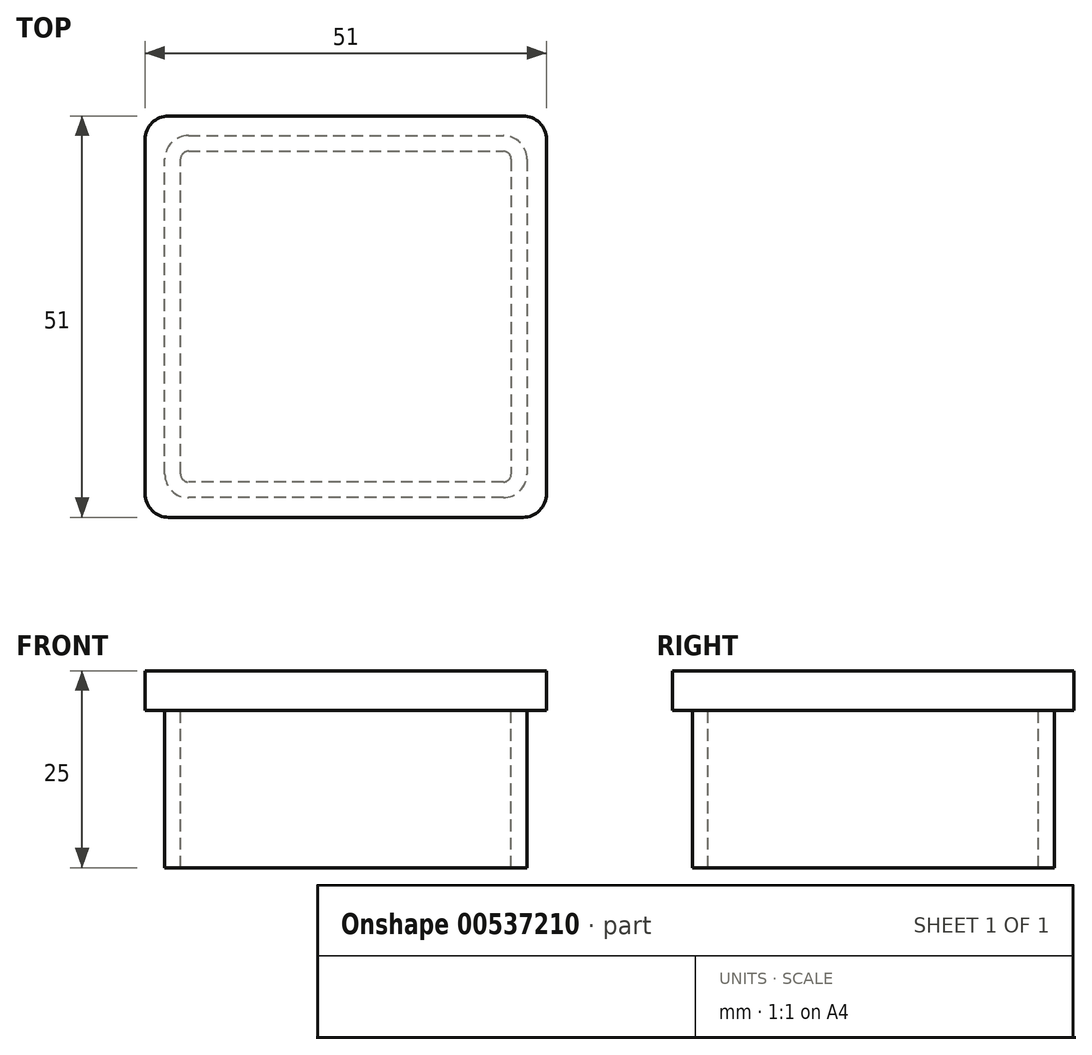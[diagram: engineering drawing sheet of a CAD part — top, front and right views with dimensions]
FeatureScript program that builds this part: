
annotation { "Feature Type Name" : "Feature", "Feature Type Description" : "" }
export const myFeature = defineFeature(function(context is Context, id is Id, definition is map)
    precondition{}
    {
        {
            var Q0;
            Q0=qCreatedBy(makeId("Top.planeOp"),FACE);
            var sketch = newSketch(context, id + "F0", { "sketchPlane" : qUnion([Q0])});
            skLineSegment(sketch, "E0.bottom", {"start": v(-22.5, -25.5) * mm, "end": v(22.5, -25.5) * mm});
            skLineSegment(sketch, "E0.top", {"start": v(-22.5, 25.5) * mm, "end": v(22.5, 25.5) * mm});
            skLineSegment(sketch, "E0.left", {"start": v(-25.5, -22.5) * mm, "end": v(-25.5, 22.5) * mm});
            skLineSegment(sketch, "E0.right", {"start": v(25.5, -22.5) * mm, "end": v(25.5, 22.5) * mm});
            skPoint(sketch, "E1.visualSharp", {"position": v(-25.5, 25.5) * mm});
            skArc(sketch, "E1.filletArc", {"start": v(-22.5, 25.5) * mm, "mid": v(-24.62, 24.62) * mm, "end": v(-25.5, 22.5) * mm});
            skPoint(sketch, "E2.visualSharp", {"position": v(25.5, 25.5) * mm});
            skArc(sketch, "E2.filletArc", {"start": v(25.5, 22.5) * mm, "mid": v(24.62, 24.62) * mm, "end": v(22.5, 25.5) * mm});
            skPoint(sketch, "E3.visualSharp", {"position": v(25.5, -25.5) * mm});
            skArc(sketch, "E3.filletArc", {"start": v(22.5, -25.5) * mm, "mid": v(24.62, -24.62) * mm, "end": v(25.5, -22.5) * mm});
            skPoint(sketch, "E4.visualSharp", {"position": v(-25.5, -25.5) * mm});
            skArc(sketch, "E4.filletArc", {"start": v(-25.5, -22.5) * mm, "mid": v(-24.62, -24.62) * mm, "end": v(-22.5, -25.5) * mm});
            skSolve(sketch);
        }
        {
            var Q0;
            Q0=makeQuery(id+"F0.imprint","IMPRINT",FACE,{"disambiguationData":[TD([[makeQuery(id+"F0.imprint","IMPRINT",EDGE,{"derivedFrom":sQuery(id+"F0.wireOp",EDGE,"E0.bottom")}),1.0]])]});
            extrude(context, id + "F1", {"entities" : qUnion([Q0]), "depth" : 5 * mm, "offsetDistance" : 25 * mm});
        }
        {
            var Q0;
            Q0=makeQuery(id+"F1.opExtrude","CAP_FACE",FACE,{"disambiguationData":[OSD([sQuery(id+"F0.wireOp",EDGE,"E0.bottom"),sQuery(id+"F0.wireOp",EDGE,"E0.top"),sQuery(id+"F0.wireOp",EDGE,"E0.left"),sQuery(id+"F0.wireOp",EDGE,"E0.right"),sQuery(id+"F0.wireOp",EDGE,"E1.filletArc"),sQuery(id+"F0.wireOp",EDGE,"E2.filletArc"),sQuery(id+"F0.wireOp",EDGE,"E3.filletArc"),sQuery(id+"F0.wireOp",EDGE,"E4.filletArc")])],"isStart":true});
            var sketch = newSketch(context, id + "F2", { "sketchPlane" : qUnion([Q0])});
            skLineSegment(sketch, "E5.0", {"start": v(-20, -23) * mm, "end": v(20, -23) * mm});
            skLineSegment(sketch, "E5.1", {"start": v(-23, 20) * mm, "end": v(-23, -20) * mm});
            skLineSegment(sketch, "E5.2", {"start": v(20, 23) * mm, "end": v(-20, 23) * mm});
            skLineSegment(sketch, "E5.3", {"start": v(23, -20) * mm, "end": v(23, 20) * mm});
            skPoint(sketch, "E6.visualSharp", {"position": v(-23, 23) * mm});
            skArc(sketch, "E6.filletArc", {"start": v(-20, 23) * mm, "mid": v(-22.12, 22.12) * mm, "end": v(-23, 20) * mm});
            skPoint(sketch, "E7.visualSharp", {"position": v(23, 23) * mm});
            skArc(sketch, "E7.filletArc", {"start": v(23, 20) * mm, "mid": v(22.12, 22.12) * mm, "end": v(20, 23) * mm});
            skPoint(sketch, "E8.visualSharp", {"position": v(23, -23) * mm});
            skArc(sketch, "E8.filletArc", {"start": v(20, -23) * mm, "mid": v(22.12, -22.12) * mm, "end": v(23, -20) * mm});
            skPoint(sketch, "E9.visualSharp", {"position": v(-23, -23) * mm});
            skArc(sketch, "E9.filletArc", {"start": v(-23, -20) * mm, "mid": v(-22.12, -22.12) * mm, "end": v(-20, -23) * mm});
            skArc(sketch, "E10.0", {"start": v(21, 20) * mm, "mid": v(20.7, 20.7) * mm, "end": v(20, 21) * mm});
            skLineSegment(sketch, "E10.1", {"start": v(21, -20) * mm, "end": v(21, 20) * mm});
            skLineSegment(sketch, "E10.2", {"start": v(20, 21) * mm, "end": v(-20, 21) * mm});
            skArc(sketch, "E10.3", {"start": v(20, -21) * mm, "mid": v(20.7, -20.7) * mm, "end": v(21, -20) * mm});
            skArc(sketch, "E10.4", {"start": v(-20, 21) * mm, "mid": v(-20.7, 20.7) * mm, "end": v(-21, 20) * mm});
            skLineSegment(sketch, "E10.5", {"start": v(-21, 20) * mm, "end": v(-21, -20) * mm});
            skArc(sketch, "E10.6", {"start": v(-21, -20) * mm, "mid": v(-20.7, -20.7) * mm, "end": v(-20, -21) * mm});
            skLineSegment(sketch, "E10.7", {"start": v(-20, -21) * mm, "end": v(20, -21) * mm});
            skSolve(sketch);
        }
        {
            var Q0;
            Q0=makeQuery(id+"F2.imprint","IMPRINT",FACE,{"disambiguationData":[TD([[makeQuery(id+"F2.imprint","IMPRINT",EDGE,{"derivedFrom":sQuery(id+"F2.wireOp",EDGE,"E5.0")}),1.0]])]});
            extrude(context, id + "F3", {"entities" : qUnion([Q0]), "operationType" : NewBodyOperationType.ADD, "depth" : 20 * mm, "offsetDistance" : 25 * mm});
        }
    });
